# Revit family: ØS Søjler Spæncom
name_source: partatom
category: Structural Columns
revit_build: Autodesk Revit 2014 (Build: 20130308_1515(x64)
units: mm (PartAtom-declared; Revit-internal decimal feet)

## types (14) — shared parameters
Manufacturer = Spæncom

## per-type parameters (varying)
| type | Diameter | Radius |
| ØS 18 | 180 mm  [stored 0.590551 ft] | 90 mm  [stored 0.295276 ft] |
| ØS 20 | 200 mm  [stored 0.656168 ft] | 100 mm  [stored 0.328084 ft] |
| ØS22,5 | 225 mm  [stored 0.738189 ft] | 113 mm |
| ØS 25 | 250 mm  [stored 0.82021 ft] | 125 mm  [stored 0.410105 ft] |
| ØS 28 | 280 mm  [stored 0.918635 ft] | 140 mm  [stored 0.459318 ft] |
| ØS 30 | 300 mm | 150 mm |
| ØS 32 | 320 mm  [stored 1.04987 ft] | 160 mm  [stored 0.524934 ft] |
| ØS 35 | 350 mm  [stored 1.14829 ft] | 175 mm  [stored 0.574147 ft] |
| ØS 36 | 360 mm  [stored 1.1811 ft] | 180 mm  [stored 0.590551 ft] |
| ØS 40 | 400 mm  [stored 1.31234 ft] | 200 mm  [stored 0.656168 ft] |
| ØS 45 | 450 mm  [stored 1.47638 ft] | 225 mm  [stored 0.738189 ft] |
| ØS 50 | 500 mm  [stored 1.64042 ft] | 250 mm  [stored 0.82021 ft] |
| ØS 60 | 600 mm | 300 mm |
| ØS 75 | 750 mm  [stored 2.46063 ft] | 375 mm  [stored 1.23031 ft] |

note: [stored X ft] marks values corroborated as IEEE doubles in the binary element streams (Revit-internal decimal feet)

## geometry (parser evidence)
native form markers: Sweep x6
no freeform markers — native parametric forms only
